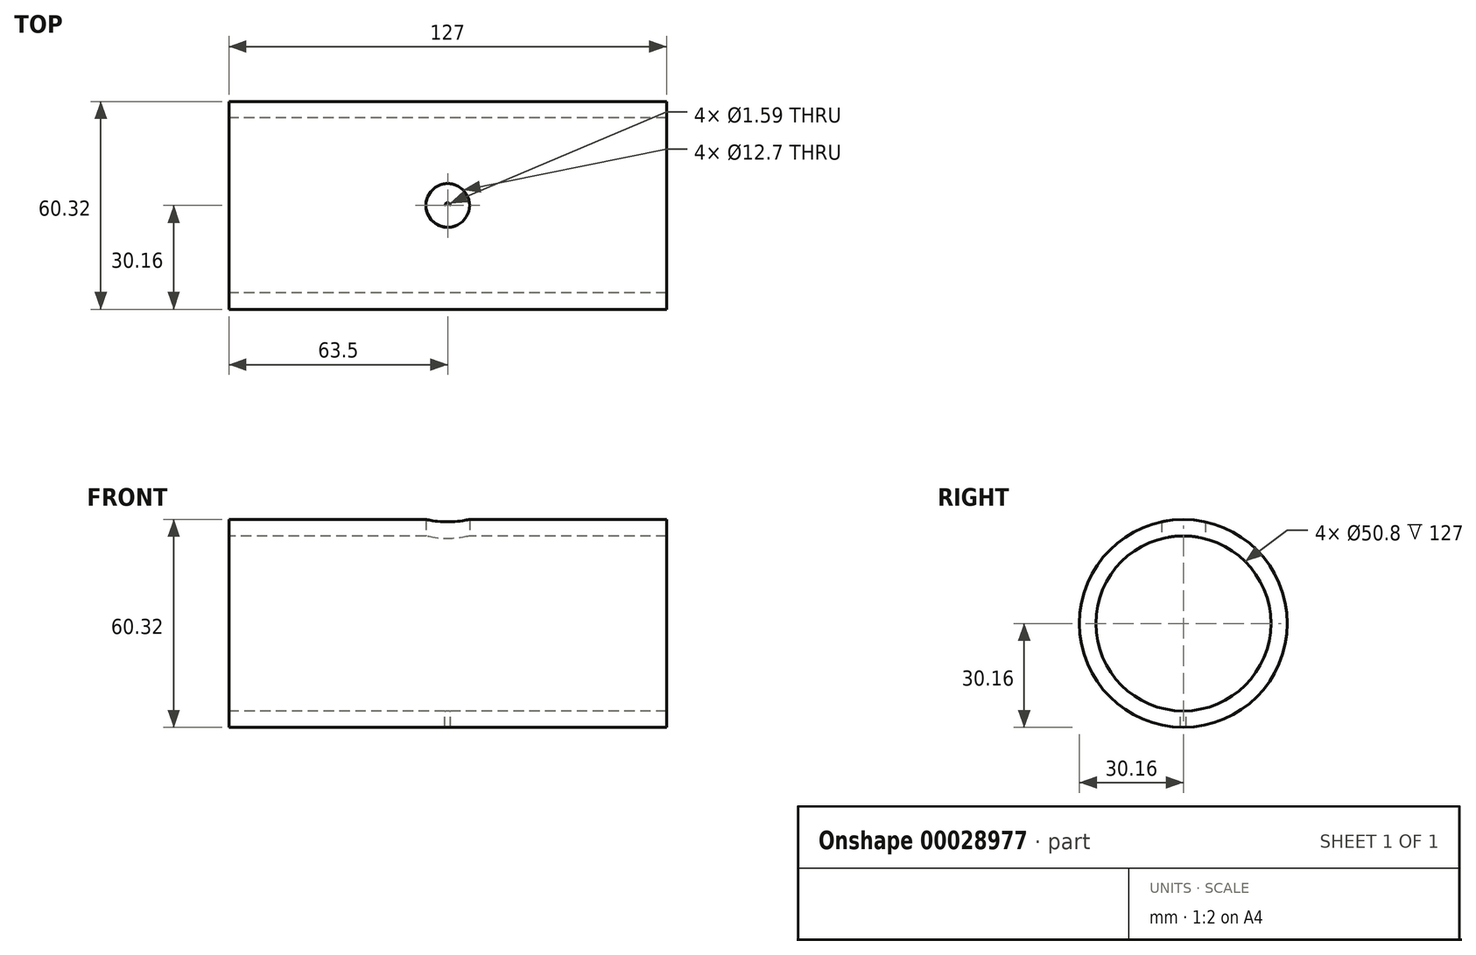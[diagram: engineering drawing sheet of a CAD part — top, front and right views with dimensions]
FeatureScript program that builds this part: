
annotation { "Feature Type Name" : "Feature", "Feature Type Description" : "" }
export const myFeature = defineFeature(function(context is Context, id is Id, definition is map)
    precondition{}
    {
        {
            var Q0;
            Q0=qCreatedBy(makeId("Right.planeOp"),FACE);
            var sketch = newSketch(context, id + "F0", { "sketchPlane" : qUnion([Q0])});
            skCircle(sketch, "E0", {"center": v(0, 0) * mm, "radius": 25.4 * mm});
            skCircle(sketch, "E1", {"center": v(0, 0) * mm, "radius": 30.16 * mm});
            skSolve(sketch);
        }
        {
            var Q0;
            Q0 = qSketchRegion(id + "F0", true);
            extrude(context, id + "F1", {"entities" : qUnion([Q0]), "depth" : 127 * mm});
        }
        {
            var Q0;
            Q0=qCreatedBy(makeId("Top.planeOp"),FACE);
            var sketch = newSketch(context, id + "F2", { "sketchPlane" : qUnion([Q0])});
            skPoint(sketch, "E2", {"position": v(63.5, 0) * mm});
            skSolve(sketch);
        }
        {
            var Q0;
            Q0=sQuery(id+"F2.wireOp",VERTEX,"E2");
            var Q1;
            Q1=makeQuery(id+"F1.opExtrude","SWEPT_BODY",BODY,{"disambiguationData":[OSD([sQuery(id+"F0.wireOp",EDGE,"E0"),sQuery(id+"F0.wireOp",EDGE,"E1")])]});
            hole(context, id + "F3", {"style" : HoleStyle.SIMPLE, "holeDiameter" : 1.59 * mm, "endStyle" : HoleEndStyle.THROUGH, "locations" : qUnion([Q0]), "scope" : qUnion([Q1])});
        }
        {
            var Q0;
            Q0=qCreatedBy(makeId("Top.planeOp"),FACE);
            var sketch = newSketch(context, id + "F4", { "sketchPlane" : qUnion([Q0])});
            skPoint(sketch, "E3", {"position": v(63.5, 0) * mm});
            skSolve(sketch);
        }
        {
            var Q0;
            Q0=sQuery(id+"F4.wireOp",VERTEX,"E3");
            var Q1;
            Q1=makeQuery(id+"F1.opExtrude","SWEPT_BODY",BODY,{"disambiguationData":[OSD([sQuery(id+"F0.wireOp",EDGE,"E0"),sQuery(id+"F0.wireOp",EDGE,"E1")])]});
            hole(context, id + "F5", {"style" : HoleStyle.SIMPLE, "holeDiameter" : 12.7 * mm, "endStyle" : HoleEndStyle.THROUGH, "oppositeDirection" : true, "locations" : qUnion([Q0]), "scope" : qUnion([Q1])});
        }
    });
